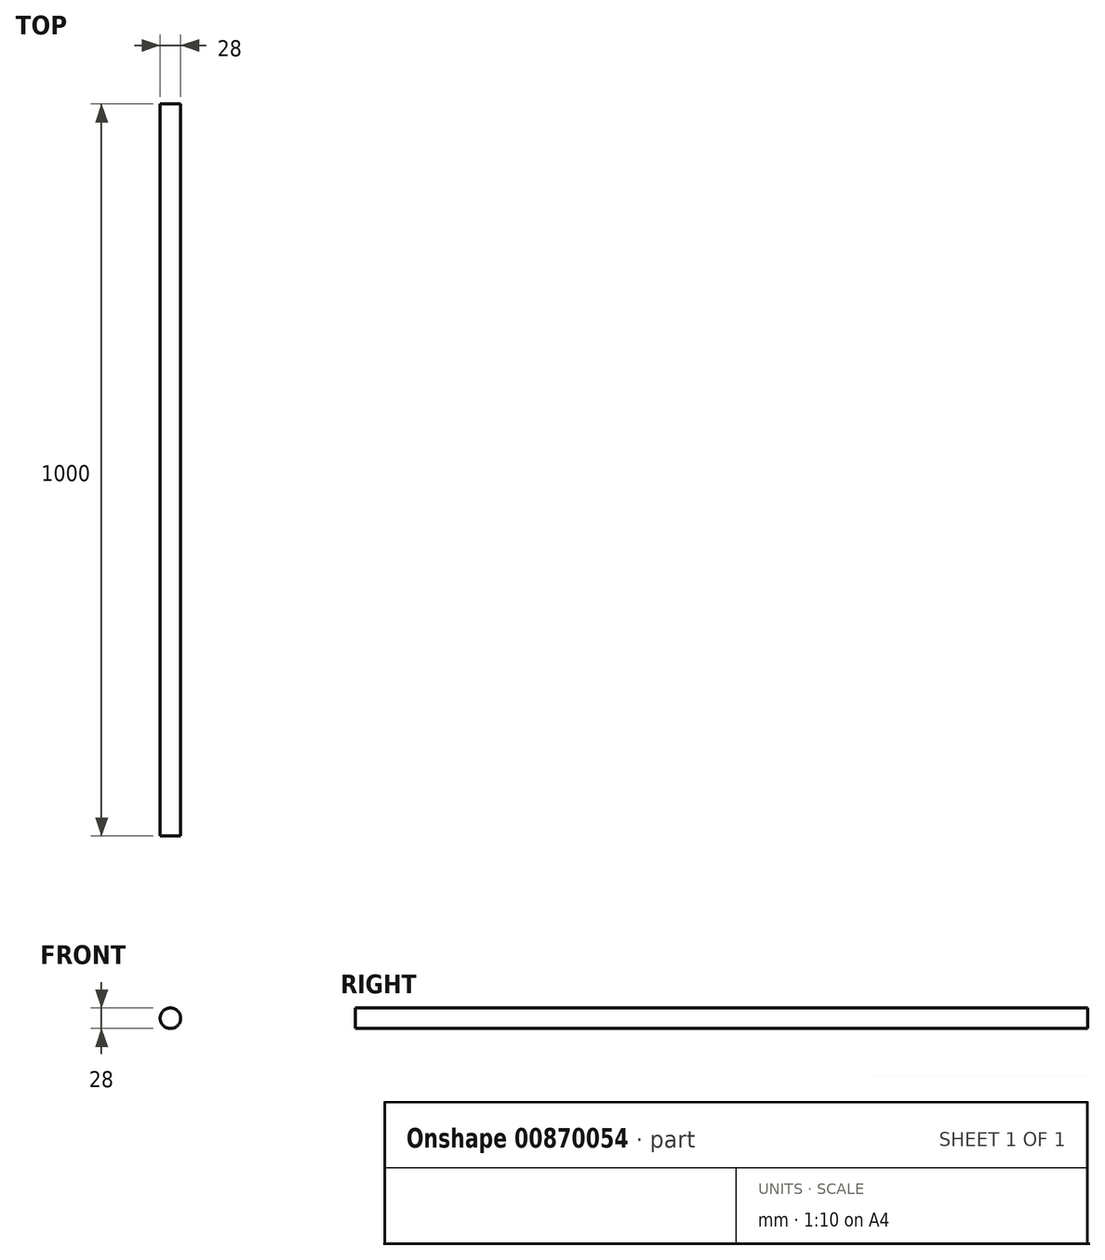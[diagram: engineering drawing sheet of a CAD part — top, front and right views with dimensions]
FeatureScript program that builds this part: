
annotation { "Feature Type Name" : "Feature", "Feature Type Description" : "" }
export const myFeature = defineFeature(function(context is Context, id is Id, definition is map)
    precondition{}
    {
        {
            var Q0;
            Q0=qCreatedBy(makeId("Front.planeOp"),FACE);
            var sketch = newSketch(context, id + "F0", { "sketchPlane" : qUnion([Q0])});
            skCircle(sketch, "E0", {"center": v(0, 0) * mm, "radius": 14 * mm});
            skSolve(sketch);
        }
        {
            var Q0;
            Q0 = qSketchRegion(id + "F0", true);
            extrude(context, id + "F1", {"entities" : qUnion([Q0]), "endBound" : BoundingType.SYMMETRIC, "depth" : 1000 * mm, "offsetDistance" : 25.4 * mm});
        }
    });
